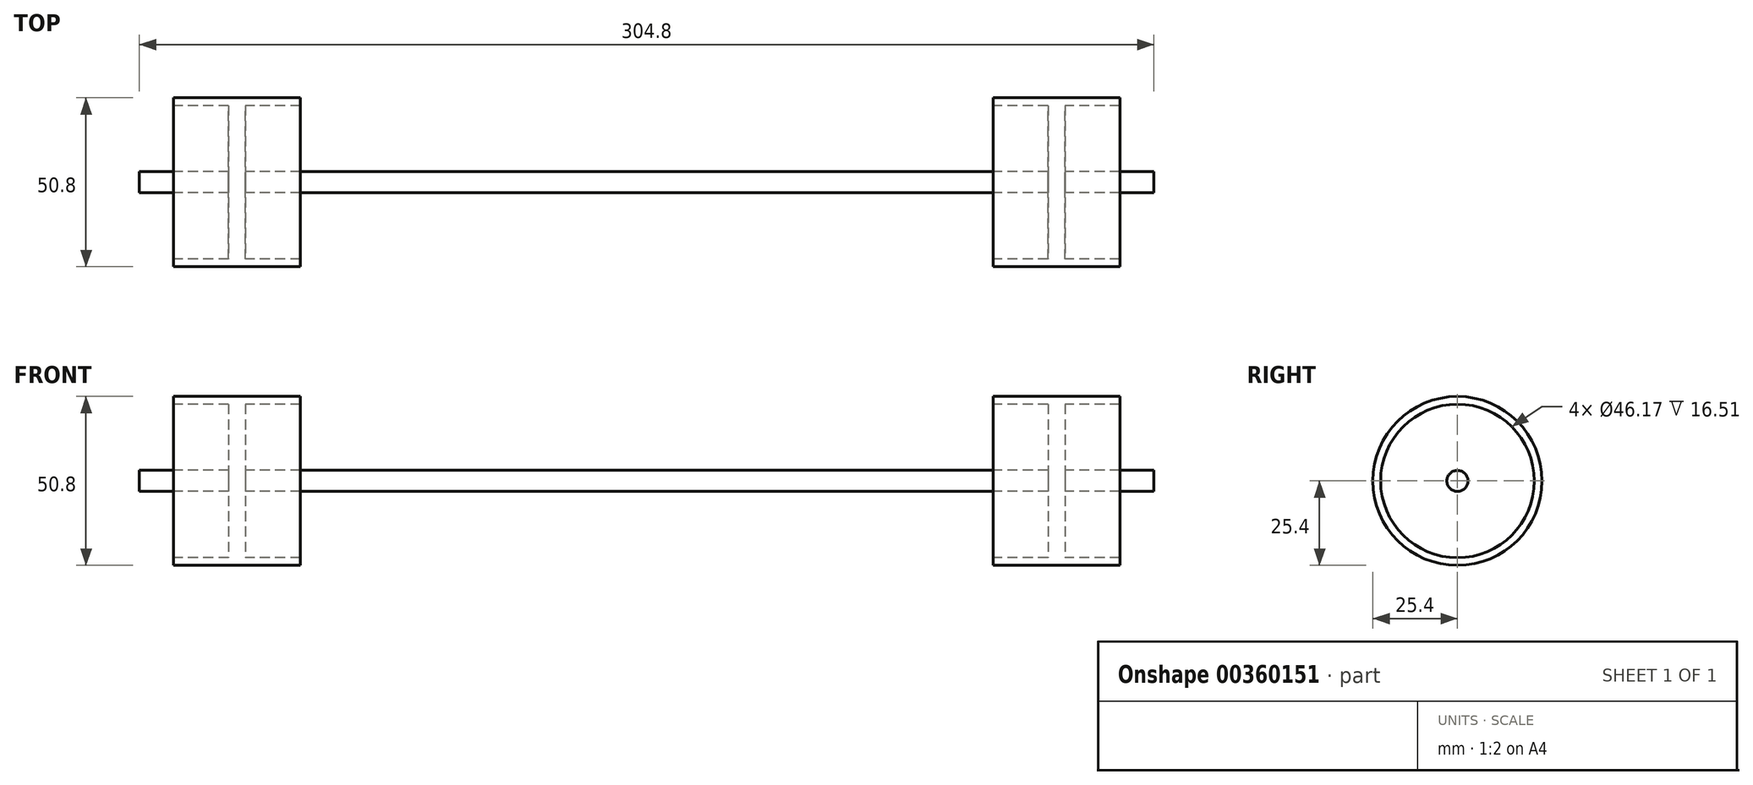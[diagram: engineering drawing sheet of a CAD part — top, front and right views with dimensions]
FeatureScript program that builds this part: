
annotation { "Feature Type Name" : "Feature", "Feature Type Description" : "" }
export const myFeature = defineFeature(function(context is Context, id is Id, definition is map)
    precondition{}
    {
        {
            var Q0;
            Q0=qCreatedBy(makeId("Front.planeOp"),FACE);
            var sketch = newSketch(context, id + "F0", { "sketchPlane" : qUnion([Q0])});
            skLineSegment(sketch, "E0", {"start": v(0, 3.17) * mm, "end": v(104.05, 3.18) * mm});
            skLineSegment(sketch, "E1", {"start": v(104.05, 23.08) * mm, "end": v(104.05, 25.4) * mm});
            skLineSegment(sketch, "E2", {"start": v(104.05, 25.4) * mm, "end": v(142.15, 25.4) * mm});
            skLineSegment(sketch, "E3", {"start": v(142.15, 25.4) * mm, "end": v(142.15, 23.08) * mm});
            skLineSegment(sketch, "E4", {"start": v(142.15, 3.18) * mm, "end": v(152.4, 3.18) * mm});
            skLineSegment(sketch, "E5", {"start": v(152.4, 3.18) * mm, "end": v(152.4, 0) * mm});
            skLineSegment(sketch, "E6", {"start": v(152.4, 0) * mm, "end": v(0, 0) * mm});
            skLineSegment(sketch, "E7", {"start": v(104.05, 23.08) * mm, "end": v(120.56, 23.08) * mm});
            skLineSegment(sketch, "E8", {"start": v(120.56, 23.08) * mm, "end": v(120.56, 3.18) * mm});
            skLineSegment(sketch, "E9", {"start": v(142.15, 23.08) * mm, "end": v(125.64, 23.08) * mm});
            skLineSegment(sketch, "E10", {"start": v(125.64, 23.08) * mm, "end": v(125.64, 3.18) * mm});
            skLineSegment(sketch, "E11", {"start": v(104.05, 3.18) * mm, "end": v(120.56, 3.18) * mm});
            skLineSegment(sketch, "E12", {"start": v(125.64, 3.18) * mm, "end": v(142.15, 3.18) * mm});
            skLineSegment(sketch, "E13.MirrorCS", {"start": v(0, 3.17) * mm, "end": v(-104.05, 3.18) * mm});
            skLineSegment(sketch, "E14.MirrorCS", {"start": v(-152.4, 0) * mm, "end": v(0, 0) * mm});
            skLineSegment(sketch, "E15.MirrorCS", {"start": v(-120.56, 23.08) * mm, "end": v(-120.56, 3.18) * mm});
            skLineSegment(sketch, "E16.MirrorCS", {"start": v(-104.05, 23.08) * mm, "end": v(-120.56, 23.08) * mm});
            skLineSegment(sketch, "E17.MirrorCS", {"start": v(-104.05, 23.08) * mm, "end": v(-104.05, 25.4) * mm});
            skLineSegment(sketch, "E18.MirrorCS", {"start": v(-104.05, 25.4) * mm, "end": v(-142.15, 25.4) * mm});
            skLineSegment(sketch, "E19.MirrorCS", {"start": v(-142.15, 25.4) * mm, "end": v(-142.15, 23.08) * mm});
            skLineSegment(sketch, "E20.MirrorCS", {"start": v(-125.64, 23.08) * mm, "end": v(-125.64, 3.18) * mm});
            skLineSegment(sketch, "E21.MirrorCS", {"start": v(-125.64, 3.18) * mm, "end": v(-142.15, 3.18) * mm});
            skLineSegment(sketch, "E22.MirrorCS", {"start": v(-142.15, 3.18) * mm, "end": v(-152.4, 3.18) * mm});
            skLineSegment(sketch, "E23.MirrorCS", {"start": v(-104.05, 3.18) * mm, "end": v(-120.56, 3.18) * mm});
            skLineSegment(sketch, "E24.MirrorCS", {"start": v(-152.4, 3.18) * mm, "end": v(-152.4, 0) * mm});
            skLineSegment(sketch, "E25.MirrorCS", {"start": v(-142.15, 23.08) * mm, "end": v(-125.64, 23.08) * mm});
            skSolve(sketch);
        }
        {
            var Q0;
            Q0=qCreatedBy(makeId("Front.planeOp"),FACE);
            var sketch = newSketch(context, id + "F1", { "sketchPlane" : qUnion([Q0])});
            skLineSegment(sketch, "E26", {"start": v(-171.47, 0) * mm, "end": v(167.43, 0) * mm});
            skSolve(sketch);
        }
        {
            var Q0;
            Q0=makeQuery(id+"F0.imprint","IMPRINT",FACE,{"disambiguationData":[TD([[makeQuery(id+"F0.imprint","IMPRINT",EDGE,{"derivedFrom":sQuery(id+"F0.wireOp",EDGE,"E0")}),-1.0]])]});
            var Q1;
            Q1=sQuery(id+"F1.wireOp",EDGE,"E26");
            revolve(context, id + "F2", {"entities" : qUnion([Q0]), "axis" : qUnion([Q1]), "revolveType" : RevolveType.FULL});
        }
    });
